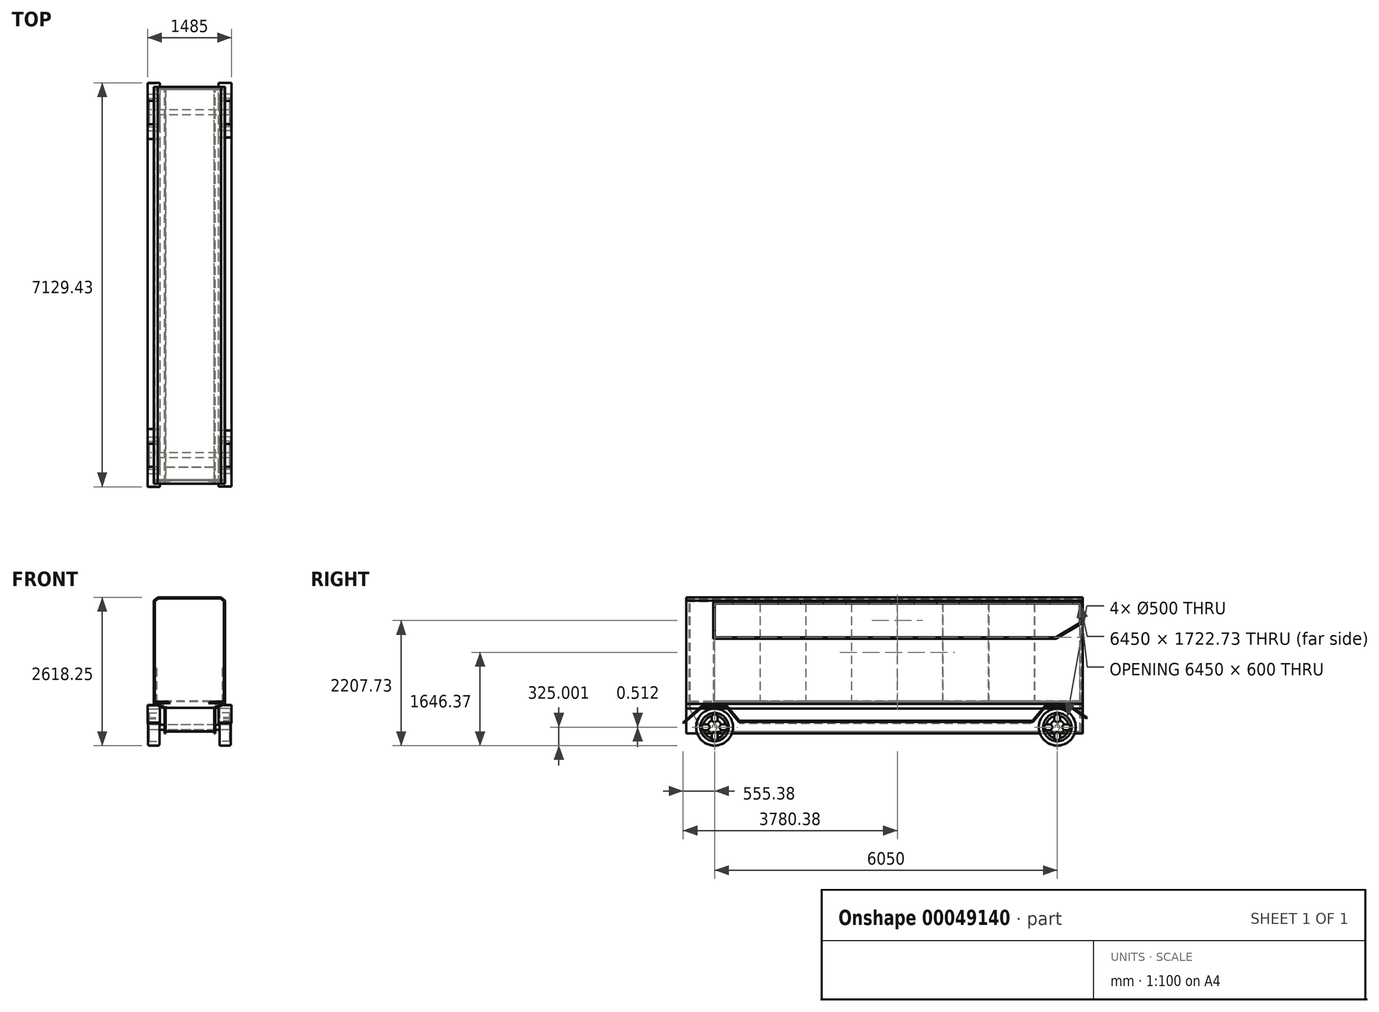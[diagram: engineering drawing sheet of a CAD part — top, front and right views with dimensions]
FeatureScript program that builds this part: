
annotation { "Feature Type Name" : "Feature", "Feature Type Description" : "" }
export const myFeature = defineFeature(function(context is Context, id is Id, definition is map)
    precondition{}
    {
        {
            var Q0;
            Q0=qCreatedBy(makeId("Front.planeOp"),FACE);
            var sketch = newSketch(context, id + "F0", { "sketchPlane" : qUnion([Q0])});
            skLineSegment(sketch, "E0", {"start": v(0, 0) * mm, "end": v(0, 1850) * mm, "construction": true});
            skLineSegment(sketch, "E1", {"start": v(-548.86, 1850) * mm, "end": v(548.86, 1850) * mm});
            skLineSegment(sketch, "E2", {"start": v(-610, 1800) * mm, "end": v(-610, 0) * mm});
            skLineSegment(sketch, "E3", {"start": v(610, 1800) * mm, "end": v(610, 0) * mm});
            skLineSegment(sketch, "E4", {"start": v(-548.86, 1850) * mm, "end": v(-610, 1800) * mm});
            skLineSegment(sketch, "E5", {"start": v(548.86, 1850) * mm, "end": v(610, 1800) * mm});
            skLineSegment(sketch, "E6", {"start": v(-610, 0) * mm, "end": v(-421.1, -80) * mm});
            skLineSegment(sketch, "E7", {"start": v(-421.1, -80) * mm, "end": v(-421.1, -530) * mm});
            skLineSegment(sketch, "E8", {"start": v(610, 0) * mm, "end": v(438.57, -80) * mm});
            skLineSegment(sketch, "E9", {"start": v(438.57, -80) * mm, "end": v(438.57, -530) * mm});
            skLineSegment(sketch, "E10.0", {"start": v(-441.1, -93.25) * mm, "end": v(-441.1, -530) * mm});
            skLineSegment(sketch, "E10.1", {"start": v(-630, -13.25) * mm, "end": v(-441.1, -93.25) * mm});
            skLineSegment(sketch, "E10.2", {"start": v(-630, 1809.48) * mm, "end": v(-630, -13.25) * mm});
            skLineSegment(sketch, "E10.3", {"start": v(-556, 1870) * mm, "end": v(-630, 1809.48) * mm});
            skLineSegment(sketch, "E10.4", {"start": v(-556, 1870) * mm, "end": v(556, 1870) * mm});
            skLineSegment(sketch, "E10.5", {"start": v(458.57, -92.74) * mm, "end": v(458.57, -530) * mm});
            skLineSegment(sketch, "E10.6", {"start": v(630, -12.74) * mm, "end": v(458.57, -92.74) * mm});
            skLineSegment(sketch, "E10.7", {"start": v(630, 1809.48) * mm, "end": v(630, -12.74) * mm});
            skLineSegment(sketch, "E10.8", {"start": v(556, 1870) * mm, "end": v(630, 1809.48) * mm});
            skLineSegment(sketch, "E11", {"start": v(-441.1, -530) * mm, "end": v(-421.1, -530) * mm});
            skLineSegment(sketch, "E12", {"start": v(438.57, -530) * mm, "end": v(458.57, -530) * mm});
            skSolve(sketch);
        }
        {
            var Q0;
            Q0 = qSketchRegion(id + "F0", true);
            extrude(context, id + "F1", {"entities" : qUnion([Q0]), "depth" : 7000 * mm});
        }
        {
            var Q0;
            Q0=makeQuery(id+"F1.opExtrude","SWEPT_FACE",FACE,{"disambiguationData":[OSD([sQuery(id+"F0.wireOp",EDGE,"E3")])]});
            var sketch = newSketch(context, id + "F2", { "sketchPlane" : qUnion([Q0])});
            skLineSegment(sketch, "E13.bottom", {"start": v(6930, 1800) * mm, "end": v(6950, 1800) * mm});
            skLineSegment(sketch, "E13.top", {"start": v(6930, 0) * mm, "end": v(6950, 0) * mm});
            skLineSegment(sketch, "E13.left", {"start": v(6930, 1800) * mm, "end": v(6930, 0) * mm});
            skLineSegment(sketch, "E13.right", {"start": v(6950, 1800) * mm, "end": v(6950, 0) * mm});
            skSolve(sketch);
        }
        {
            var Q0;
            Q0 = qSketchRegion(id + "F2", true);
            extrude(context, id + "F3", {"entities" : qUnion([Q0]), "endBound" : BoundingType.UP_TO_NEXT, "depth" : 25 * mm});
        }
        {
            var Q0;
            Q0=makeQuery(id+"F3.opExtrude","SWEPT_FACE",FACE,{"disambiguationData":[OSD([sQuery(id+"F2.wireOp",EDGE,"E13.right")])]});
            var sketch = newSketch(context, id + "F4", { "sketchPlane" : qUnion([Q0])});
            skLineSegment(sketch, "E14", {"start": v(-610, 1800) * mm, "end": v(610, 1800) * mm});
            skLineSegment(sketch, "E15", {"start": v(610, 1800) * mm, "end": v(549.02, 1850.83) * mm});
            skLineSegment(sketch, "E16", {"start": v(549.02, 1850.83) * mm, "end": v(-548.33, 1850.83) * mm});
            skLineSegment(sketch, "E17", {"start": v(-548.33, 1850.83) * mm, "end": v(-610, 1800) * mm});
            skSolve(sketch);
        }
        {
            var Q0;
            Q0 = qSketchRegion(id + "F4", true);
            extrude(context, id + "F5", {"entities" : qUnion([Q0]), "oppositeDirection" : true, "depth" : 20 * mm});
        }
        {
            var Q0;
            Q0=makeQuery(id+"F5.boolean.opBoolean","MERGE",FACE,{"derivedFrom":[makeQuery(id+"F3.opExtrude","SWEPT_FACE",FACE,{"disambiguationData":[OSD([sQuery(id+"F2.wireOp",EDGE,"E13.right")])]}),makeQuery(id+"F5.opExtrude","CAP_FACE",FACE,{"disambiguationData":[OSD([sQuery(id+"F4.wireOp",EDGE,"E14"),sQuery(id+"F4.wireOp",EDGE,"E15"),sQuery(id+"F4.wireOp",EDGE,"E16"),sQuery(id+"F4.wireOp",EDGE,"E17")])],"isStart":true})]});
            var sketch = newSketch(context, id + "F6", { "sketchPlane" : qUnion([Q0])});
            skLineSegment(sketch, "E18", {"start": v(-610, 0) * mm, "end": v(610, 0) * mm});
            skLineSegment(sketch, "E19", {"start": v(610, 0) * mm, "end": v(438.54, -79.98) * mm});
            skLineSegment(sketch, "E20", {"start": v(438.54, -79.98) * mm, "end": v(438.54, -80.03) * mm});
            skLineSegment(sketch, "E21", {"start": v(438.54, -80.03) * mm, "end": v(-421.13, -80.03) * mm});
            skLineSegment(sketch, "E22", {"start": v(-421.13, -80.03) * mm, "end": v(-421.13, -79.98) * mm});
            skLineSegment(sketch, "E23", {"start": v(-421.13, -79.98) * mm, "end": v(-610, 0) * mm});
            skSolve(sketch);
        }
        {
            var Q0;
            Q0 = qSketchRegion(id + "F6", true);
            extrude(context, id + "F7", {"entities" : qUnion([Q0]), "oppositeDirection" : true, "depth" : 20 * mm});
        }
        {
            var Q0;
            Q0=makeQuery(id+"F1.opExtrude","SWEPT_FACE",FACE,{"disambiguationData":[OSD([sQuery(id+"F0.wireOp",EDGE,"E10.2")])]});
            var sketch = newSketch(context, id + "F8", { "sketchPlane" : qUnion([Q0])});
            skLineSegment(sketch, "E24.bottom", {"start": v(50, 1759.48) * mm, "end": v(6500, 1759.48) * mm});
            skLineSegment(sketch, "E24.top", {"start": v(50, 36.75) * mm, "end": v(6500, 36.75) * mm});
            skLineSegment(sketch, "E24.left", {"start": v(50, 1759.48) * mm, "end": v(50, 36.75) * mm});
            skLineSegment(sketch, "E24.right", {"start": v(6500, 1759.48) * mm, "end": v(6500, 36.75) * mm});
            skSolve(sketch);
        }
        {
            var Q0;
            Q0=makeQuery(id+"F8.imprint","IMPRINT",FACE,{"disambiguationData":[TD([[makeQuery(id+"F8.imprint","IMPRINT",EDGE,{"derivedFrom":sQuery(id+"F8.wireOp",EDGE,"E24.bottom")}),-1.0]])]});
            extrude(context, id + "F9", {"entities" : qUnion([Q0]), "operationType" : NewBodyOperationType.REMOVE, "oppositeDirection" : true, "depth" : 25 * mm});
        }
        {
            var Q0;
            Q0=makeQuery(id+"F3.opExtrude","SWEPT_BODY",BODY,{"disambiguationData":[OSD([sQuery(id+"F2.wireOp",EDGE,"E13.bottom"),sQuery(id+"F2.wireOp",EDGE,"E13.top"),sQuery(id+"F2.wireOp",EDGE,"E13.left"),sQuery(id+"F2.wireOp",EDGE,"E13.right")])]});
            var Q1;
            Q1=makeQuery(id+"F7.opExtrude","SWEPT_BODY",BODY,{"disambiguationData":[OSD([sQuery(id+"F6.wireOp",EDGE,"E18"),sQuery(id+"F6.wireOp",EDGE,"E19"),sQuery(id+"F6.wireOp",EDGE,"E20"),sQuery(id+"F6.wireOp",EDGE,"E21"),sQuery(id+"F6.wireOp",EDGE,"E22"),sQuery(id+"F6.wireOp",EDGE,"E23")])]});
            var Q2;
            Q2=makeQuery(id+"F5.opExtrude","SWEPT_BODY",BODY,{"disambiguationData":[OSD([sQuery(id+"F4.wireOp",EDGE,"E14"),sQuery(id+"F4.wireOp",EDGE,"E15"),sQuery(id+"F4.wireOp",EDGE,"E16"),sQuery(id+"F4.wireOp",EDGE,"E17")])]});
            booleanBodies(context, id + "F10", {"operationType" : BooleanOperationType.UNION, "tools" : qUnion([Q0, Q1, Q2])});
        }
        {
            var Q0;
            Q0=makeQuery(id+"F1.opExtrude","SWEPT_FACE",FACE,{"disambiguationData":[OSD([sQuery(id+"F0.wireOp",EDGE,"E2")])]});
            var sketch = newSketch(context, id + "F11", { "sketchPlane" : qUnion([Q0])});
            skLineSegment(sketch, "E25.bottom", {"start": v(-50, 1800) * mm, "end": v(-30, 1800) * mm});
            skLineSegment(sketch, "E25.top", {"start": v(-50, 0) * mm, "end": v(-30, 0) * mm});
            skLineSegment(sketch, "E25.left", {"start": v(-50, 1800) * mm, "end": v(-50, 0) * mm});
            skLineSegment(sketch, "E25.right", {"start": v(-30, 1800) * mm, "end": v(-30, 0) * mm});
            skSolve(sketch);
        }
        {
            var Q0;
            Q0 = qSketchRegion(id + "F11", true);
            extrude(context, id + "F12", {"entities" : qUnion([Q0]), "operationType" : NewBodyOperationType.ADD, "endBound" : BoundingType.UP_TO_NEXT, "depth" : 25 * mm});
        }
        {
            var Q0;
            Q0=makeQuery(id+"F12.opExtrude","SWEPT_FACE",FACE,{"disambiguationData":[OSD([sQuery(id+"F11.wireOp",EDGE,"E25.right")])]});
            var sketch = newSketch(context, id + "F13", { "sketchPlane" : qUnion([Q0])});
            skLineSegment(sketch, "E26", {"start": v(-610, 1800) * mm, "end": v(610, 1800) * mm});
            skLineSegment(sketch, "E27", {"start": v(610, 1800) * mm, "end": v(548.9, 1850.1) * mm});
            skLineSegment(sketch, "E28", {"start": v(548.9, 1850.1) * mm, "end": v(-548.85, 1850.1) * mm});
            skLineSegment(sketch, "E29", {"start": v(-548.85, 1850.1) * mm, "end": v(-610, 1800) * mm});
            skSolve(sketch);
        }
        {
            var Q0;
            Q0 = qSketchRegion(id + "F13", true);
            extrude(context, id + "F14", {"entities" : qUnion([Q0]), "operationType" : NewBodyOperationType.ADD, "oppositeDirection" : true, "depth" : 20 * mm});
        }
        {
            var Q0;
            Q0=makeQuery(id+"F14.boolean.opBoolean","MERGE",FACE,{"derivedFrom":[makeQuery(id+"F12.opExtrude","SWEPT_FACE",FACE,{"disambiguationData":[OSD([sQuery(id+"F11.wireOp",EDGE,"E25.right")])]}),makeQuery(id+"F14.opExtrude","CAP_FACE",FACE,{"disambiguationData":[OSD([sQuery(id+"F13.wireOp",EDGE,"E26"),sQuery(id+"F13.wireOp",EDGE,"E27"),sQuery(id+"F13.wireOp",EDGE,"E28"),sQuery(id+"F13.wireOp",EDGE,"E29")])],"isStart":true})]});
            var sketch = newSketch(context, id + "F15", { "sketchPlane" : qUnion([Q0])});
            skLineSegment(sketch, "E30", {"start": v(-610, 0) * mm, "end": v(610, 0) * mm});
            skLineSegment(sketch, "E31", {"start": v(610, 0) * mm, "end": v(421.14, -80.03) * mm});
            skLineSegment(sketch, "E32", {"start": v(421.14, -80.03) * mm, "end": v(421.14, -504.23) * mm});
            skLineSegment(sketch, "E33", {"start": v(421.14, -504.23) * mm, "end": v(-438.57, -504.23) * mm});
            skLineSegment(sketch, "E34", {"start": v(-438.57, -504.23) * mm, "end": v(-438.57, -80.03) * mm});
            skLineSegment(sketch, "E35", {"start": v(-438.57, -80.03) * mm, "end": v(-610, 0) * mm});
            skSolve(sketch);
        }
        {
            var Q0;
            Q0 = qSketchRegion(id + "F15", true);
            extrude(context, id + "F16", {"entities" : qUnion([Q0]), "operationType" : NewBodyOperationType.ADD, "oppositeDirection" : true, "depth" : 20 * mm});
        }
        {
            var Q0;
            Q0=makeQuery(id+"F16.boolean.opBoolean","MERGE",FACE,{"derivedFrom":[makeQuery(id+"F14.boolean.opBoolean","MERGE",FACE,{"derivedFrom":[makeQuery(id+"F12.boolean.opBoolean","MERGE",FACE,{"derivedFrom":[makeQuery(id+"F9.boolean.opBoolean","COPY",FACE,{"derivedFrom":makeQuery(id+"F9.opExtrude","SWEPT_FACE",FACE,{"disambiguationData":[OSD([sQuery(id+"F8.wireOp",EDGE,"E24.left")])]})}),makeQuery(id+"F12.opExtrude","SWEPT_FACE",FACE,{"disambiguationData":[OSD([sQuery(id+"F11.wireOp",EDGE,"E25.left")])]})]}),makeQuery(id+"F14.opExtrude","CAP_FACE",FACE,{"disambiguationData":[OSD([sQuery(id+"F13.wireOp",EDGE,"E26"),sQuery(id+"F13.wireOp",EDGE,"E27"),sQuery(id+"F13.wireOp",EDGE,"E28"),sQuery(id+"F13.wireOp",EDGE,"E29")])],"isStart":false})]}),makeQuery(id+"F16.opExtrude","CAP_FACE",FACE,{"disambiguationData":[OSD([sQuery(id+"F15.wireOp",EDGE,"E30"),sQuery(id+"F15.wireOp",EDGE,"E31"),sQuery(id+"F15.wireOp",EDGE,"E32"),sQuery(id+"F15.wireOp",EDGE,"E33"),sQuery(id+"F15.wireOp",EDGE,"E34"),sQuery(id+"F15.wireOp",EDGE,"E35")])],"isStart":false})]});
            var sketch = newSketch(context, id + "F17", { "sketchPlane" : qUnion([Q0])});
            skLineSegment(sketch, "E36.bottom", {"start": v(610, 26.75) * mm, "end": v(-610, 26.75) * mm});
            skLineSegment(sketch, "E36.top", {"start": v(610, 36.75) * mm, "end": v(-610, 36.75) * mm});
            skLineSegment(sketch, "E36.left", {"start": v(610, 26.75) * mm, "end": v(610, 36.75) * mm});
            skLineSegment(sketch, "E36.right", {"start": v(-610, 26.75) * mm, "end": v(-610, 36.75) * mm});
            skLineSegment(sketch, "E37.bottom", {"start": v(438.57, -504.23) * mm, "end": v(-421.1, -504.23) * mm});
            skLineSegment(sketch, "E37.top", {"start": v(438.57, -494.23) * mm, "end": v(-421.1, -494.23) * mm});
            skLineSegment(sketch, "E37.left", {"start": v(438.57, -504.23) * mm, "end": v(438.57, -494.23) * mm});
            skLineSegment(sketch, "E37.right", {"start": v(-421.1, -504.23) * mm, "end": v(-421.1, -494.23) * mm});
            skSolve(sketch);
        }
        {
            var Q0;
            Q0 = qSketchRegion(id + "F17", true);
            var Q1;
            Q1=makeQuery(id+"F10.opBoolean","MERGE",FACE,{"derivedFrom":[makeQuery(id+"F3.opExtrude","SWEPT_FACE",FACE,{"disambiguationData":[OSD([sQuery(id+"F2.wireOp",EDGE,"E13.left")])]}),makeQuery(id+"F5.opExtrude","CAP_FACE",FACE,{"disambiguationData":[OSD([sQuery(id+"F4.wireOp",EDGE,"E14"),sQuery(id+"F4.wireOp",EDGE,"E15"),sQuery(id+"F4.wireOp",EDGE,"E16"),sQuery(id+"F4.wireOp",EDGE,"E17")])],"isStart":false}),makeQuery(id+"F7.opExtrude","CAP_FACE",FACE,{"disambiguationData":[OSD([sQuery(id+"F6.wireOp",EDGE,"E18"),sQuery(id+"F6.wireOp",EDGE,"E19"),sQuery(id+"F6.wireOp",EDGE,"E20"),sQuery(id+"F6.wireOp",EDGE,"E21"),sQuery(id+"F6.wireOp",EDGE,"E22"),sQuery(id+"F6.wireOp",EDGE,"E23")])],"isStart":false})]});
            extrude(context, id + "F18", {"entities" : qUnion([Q0]), "endBound" : BoundingType.UP_TO_SURFACE, "endBoundEntityFace" : qUnion([Q1]), "depth" : 6874.52 * mm});
        }
        {
            var Q0;
            Q0=makeQuery(id+"F1.opExtrude","SWEPT_BODY",BODY,{"disambiguationData":[OSD([sQuery(id+"F0.wireOp",EDGE,"E1"),sQuery(id+"F0.wireOp",EDGE,"E2"),sQuery(id+"F0.wireOp",EDGE,"E3"),sQuery(id+"F0.wireOp",EDGE,"E4"),sQuery(id+"F0.wireOp",EDGE,"E5"),sQuery(id+"F0.wireOp",EDGE,"E6"),sQuery(id+"F0.wireOp",EDGE,"E7"),sQuery(id+"F0.wireOp",EDGE,"E8"),sQuery(id+"F0.wireOp",EDGE,"E9"),sQuery(id+"F0.wireOp",EDGE,"E10.0"),sQuery(id+"F0.wireOp",EDGE,"E10.1"),sQuery(id+"F0.wireOp",EDGE,"E10.2"),sQuery(id+"F0.wireOp",EDGE,"E10.3"),sQuery(id+"F0.wireOp",EDGE,"E10.4"),sQuery(id+"F0.wireOp",EDGE,"E10.5"),sQuery(id+"F0.wireOp",EDGE,"E10.6"),sQuery(id+"F0.wireOp",EDGE,"E10.7"),sQuery(id+"F0.wireOp",EDGE,"E10.8"),sQuery(id+"F0.wireOp",EDGE,"E11"),sQuery(id+"F0.wireOp",EDGE,"E12")])]});
            var Q1;
            Q1=makeQuery(id+"F18.opExtrude","SWEPT_BODY",BODY,{"disambiguationData":[OSD([sQuery(id+"F17.wireOp",EDGE,"E36.bottom"),sQuery(id+"F17.wireOp",EDGE,"E36.top"),sQuery(id+"F17.wireOp",EDGE,"E36.left"),sQuery(id+"F17.wireOp",EDGE,"E36.right")])]});
            var Q2;
            Q2=makeQuery(id+"F18.opExtrude","SWEPT_BODY",BODY,{"disambiguationData":[OSD([sQuery(id+"F17.wireOp",EDGE,"E37.bottom"),sQuery(id+"F17.wireOp",EDGE,"E37.top"),sQuery(id+"F17.wireOp",EDGE,"E37.left"),sQuery(id+"F17.wireOp",EDGE,"E37.right")])]});
            booleanBodies(context, id + "F19", {"operationType" : BooleanOperationType.UNION, "tools" : qUnion([Q0, Q1, Q2])});
        }
        {
            var Q0;
            Q0=makeQuery(id+"F1.opExtrude","SWEPT_FACE",FACE,{"disambiguationData":[OSD([sQuery(id+"F0.wireOp",EDGE,"E10.2")])]});
            var sketch = newSketch(context, id + "F20", { "sketchPlane" : qUnion([Q0])});
            skLineSegment(sketch, "E38.bottom", {"start": v(50, 1759.48) * mm, "end": v(855, 1759.48) * mm});
            skLineSegment(sketch, "E38.top", {"start": v(50, 36.75) * mm, "end": v(855, 36.75) * mm});
            skLineSegment(sketch, "E38.left", {"start": v(50, 1759.48) * mm, "end": v(50, 36.75) * mm});
            skLineSegment(sketch, "E38.right", {"start": v(855, 1759.48) * mm, "end": v(855, 36.75) * mm});
            skLineSegment(sketch, "E39.bottom", {"start": v(857, 1759.48) * mm, "end": v(1662, 1759.48) * mm});
            skLineSegment(sketch, "E39.top", {"start": v(857, 36.75) * mm, "end": v(1662, 36.75) * mm});
            skLineSegment(sketch, "E39.left", {"start": v(857, 1759.48) * mm, "end": v(857, 36.75) * mm});
            skLineSegment(sketch, "E39.right", {"start": v(1662, 1759.48) * mm, "end": v(1662, 36.75) * mm});
            skLineSegment(sketch, "E40.bottom", {"start": v(1664, 36.75) * mm, "end": v(2469, 36.75) * mm});
            skLineSegment(sketch, "E40.top", {"start": v(1664, 1759.48) * mm, "end": v(2469, 1759.48) * mm});
            skLineSegment(sketch, "E40.left", {"start": v(1664, 36.75) * mm, "end": v(1664, 1759.48) * mm});
            skLineSegment(sketch, "E40.right", {"start": v(2469, 36.75) * mm, "end": v(2469, 1759.48) * mm});
            skLineSegment(sketch, "E41.bottom", {"start": v(2471, 1759.48) * mm, "end": v(3276, 1759.48) * mm});
            skLineSegment(sketch, "E41.top", {"start": v(2471, 36.75) * mm, "end": v(3276, 36.75) * mm});
            skLineSegment(sketch, "E41.left", {"start": v(2471, 1759.48) * mm, "end": v(2471, 36.75) * mm});
            skLineSegment(sketch, "E41.right", {"start": v(3276, 1759.48) * mm, "end": v(3276, 36.75) * mm});
            skLineSegment(sketch, "E42.bottom", {"start": v(3278, 1759.48) * mm, "end": v(4083, 1759.48) * mm});
            skLineSegment(sketch, "E42.top", {"start": v(3278, 36.75) * mm, "end": v(4083, 36.75) * mm});
            skLineSegment(sketch, "E42.left", {"start": v(3278, 1759.48) * mm, "end": v(3278, 36.75) * mm});
            skLineSegment(sketch, "E42.right", {"start": v(4083, 1759.48) * mm, "end": v(4083, 36.75) * mm});
            skLineSegment(sketch, "E43.bottom", {"start": v(4085, 1759.48) * mm, "end": v(4890, 1759.48) * mm});
            skLineSegment(sketch, "E43.top", {"start": v(4085, 36.75) * mm, "end": v(4890, 36.75) * mm});
            skLineSegment(sketch, "E43.left", {"start": v(4085, 1759.48) * mm, "end": v(4085, 36.75) * mm});
            skLineSegment(sketch, "E43.right", {"start": v(4890, 1759.48) * mm, "end": v(4890, 36.75) * mm});
            skLineSegment(sketch, "E44.bottom", {"start": v(4892, 1759.48) * mm, "end": v(5697, 1759.48) * mm});
            skLineSegment(sketch, "E44.top", {"start": v(4892, 36.75) * mm, "end": v(5697, 36.75) * mm});
            skLineSegment(sketch, "E44.left", {"start": v(4892, 1759.48) * mm, "end": v(4892, 36.75) * mm});
            skLineSegment(sketch, "E44.right", {"start": v(5697, 1759.48) * mm, "end": v(5697, 36.75) * mm});
            skLineSegment(sketch, "E45.bottom", {"start": v(5699, 1759.48) * mm, "end": v(6504, 1759.48) * mm});
            skLineSegment(sketch, "E45.top", {"start": v(5699, 36.75) * mm, "end": v(6504, 36.75) * mm});
            skLineSegment(sketch, "E45.left", {"start": v(5699, 1759.48) * mm, "end": v(5699, 36.75) * mm});
            skLineSegment(sketch, "E45.right", {"start": v(6504, 1759.48) * mm, "end": v(6504, 36.75) * mm});
            skSolve(sketch);
        }
        {
            var Q0;
            Q0 = qSketchRegion(id + "F20", true);
            extrude(context, id + "F21", {"entities" : qUnion([Q0]), "oppositeDirection" : true, "depth" : 20 * mm});
        }
        {
            var Q0;
            Q0=makeQuery(id+"F1.opExtrude","CAP_FACE",FACE,{"disambiguationData":[OSD([sQuery(id+"F0.wireOp",EDGE,"E1"),sQuery(id+"F0.wireOp",EDGE,"E2"),sQuery(id+"F0.wireOp",EDGE,"E3"),sQuery(id+"F0.wireOp",EDGE,"E4"),sQuery(id+"F0.wireOp",EDGE,"E5"),sQuery(id+"F0.wireOp",EDGE,"E6"),sQuery(id+"F0.wireOp",EDGE,"E7"),sQuery(id+"F0.wireOp",EDGE,"E8"),sQuery(id+"F0.wireOp",EDGE,"E9"),sQuery(id+"F0.wireOp",EDGE,"E10.0"),sQuery(id+"F0.wireOp",EDGE,"E10.1"),sQuery(id+"F0.wireOp",EDGE,"E10.2"),sQuery(id+"F0.wireOp",EDGE,"E10.3"),sQuery(id+"F0.wireOp",EDGE,"E10.4"),sQuery(id+"F0.wireOp",EDGE,"E10.5"),sQuery(id+"F0.wireOp",EDGE,"E10.6"),sQuery(id+"F0.wireOp",EDGE,"E10.7"),sQuery(id+"F0.wireOp",EDGE,"E10.8"),sQuery(id+"F0.wireOp",EDGE,"E11"),sQuery(id+"F0.wireOp",EDGE,"E12")])],"isStart":false});
            var sketch = newSketch(context, id + "F22", { "sketchPlane" : qUnion([Q0])});
            skLineSegment(sketch, "E46", {"start": v(-556, 1870) * mm, "end": v(556, 1870) * mm});
            skLineSegment(sketch, "E47", {"start": v(556, 1870) * mm, "end": v(630, 1809.48) * mm});
            skLineSegment(sketch, "E48", {"start": v(630, 1809.48) * mm, "end": v(630, -12.74) * mm});
            skLineSegment(sketch, "E49", {"start": v(630, -12.74) * mm, "end": v(458.57, -92.74) * mm});
            skLineSegment(sketch, "E50", {"start": v(458.57, -92.74) * mm, "end": v(458.57, -530) * mm});
            skLineSegment(sketch, "E51", {"start": v(458.57, -530) * mm, "end": v(438.57, -530) * mm});
            skLineSegment(sketch, "E52", {"start": v(438.57, -530) * mm, "end": v(438.57, -80) * mm});
            skLineSegment(sketch, "E53", {"start": v(438.57, -80) * mm, "end": v(610, 0) * mm});
            skLineSegment(sketch, "E54", {"start": v(610, 0) * mm, "end": v(610, 1800) * mm});
            skLineSegment(sketch, "E55", {"start": v(610, 1800) * mm, "end": v(548.86, 1850) * mm});
            skLineSegment(sketch, "E56", {"start": v(548.86, 1850) * mm, "end": v(-548.86, 1850) * mm});
            skLineSegment(sketch, "E57", {"start": v(-548.86, 1850) * mm, "end": v(-610, 1800) * mm});
            skLineSegment(sketch, "E58", {"start": v(-610, 1800) * mm, "end": v(-610, 0) * mm});
            skLineSegment(sketch, "E59", {"start": v(-610, 0) * mm, "end": v(-421.1, -80) * mm});
            skLineSegment(sketch, "E60", {"start": v(-421.1, -80) * mm, "end": v(-421.1, -530) * mm});
            skLineSegment(sketch, "E61", {"start": v(-421.1, -530) * mm, "end": v(-441.1, -530) * mm});
            skLineSegment(sketch, "E62", {"start": v(-441.1, -530) * mm, "end": v(-441.1, -93.25) * mm});
            skLineSegment(sketch, "E63", {"start": v(-441.1, -93.25) * mm, "end": v(-630, -13.25) * mm});
            skLineSegment(sketch, "E64", {"start": v(-630, -13.25) * mm, "end": v(-630, 1809.48) * mm});
            skLineSegment(sketch, "E65", {"start": v(-630, 1809.48) * mm, "end": v(-556, 1870) * mm});
            skSolve(sketch);
        }
        {
            var Q0;
            Q0 = qSketchRegion(id + "F22", true);
            extrude(context, id + "F23", {"entities" : qUnion([Q0]), "depth" : 1 * mm});
        }
        {
            var Q0;
            Q0=makeQuery(id+"F1.opExtrude","CAP_FACE",FACE,{"disambiguationData":[OSD([sQuery(id+"F0.wireOp",EDGE,"E1"),sQuery(id+"F0.wireOp",EDGE,"E2"),sQuery(id+"F0.wireOp",EDGE,"E3"),sQuery(id+"F0.wireOp",EDGE,"E4"),sQuery(id+"F0.wireOp",EDGE,"E5"),sQuery(id+"F0.wireOp",EDGE,"E6"),sQuery(id+"F0.wireOp",EDGE,"E7"),sQuery(id+"F0.wireOp",EDGE,"E8"),sQuery(id+"F0.wireOp",EDGE,"E9"),sQuery(id+"F0.wireOp",EDGE,"E10.0"),sQuery(id+"F0.wireOp",EDGE,"E10.1"),sQuery(id+"F0.wireOp",EDGE,"E10.2"),sQuery(id+"F0.wireOp",EDGE,"E10.3"),sQuery(id+"F0.wireOp",EDGE,"E10.4"),sQuery(id+"F0.wireOp",EDGE,"E10.5"),sQuery(id+"F0.wireOp",EDGE,"E10.6"),sQuery(id+"F0.wireOp",EDGE,"E10.7"),sQuery(id+"F0.wireOp",EDGE,"E10.8"),sQuery(id+"F0.wireOp",EDGE,"E11"),sQuery(id+"F0.wireOp",EDGE,"E12")])],"isStart":true});
            var sketch = newSketch(context, id + "F24", { "sketchPlane" : qUnion([Q0])});
            skLineSegment(sketch, "E66", {"start": v(-556, 1870) * mm, "end": v(556, 1870) * mm});
            skLineSegment(sketch, "E67", {"start": v(556, 1870) * mm, "end": v(630, 1809.48) * mm});
            skLineSegment(sketch, "E68", {"start": v(630, 1809.48) * mm, "end": v(630, -13.25) * mm});
            skLineSegment(sketch, "E69", {"start": v(630, -13.25) * mm, "end": v(441.1, -93.25) * mm});
            skLineSegment(sketch, "E70", {"start": v(441.1, -93.25) * mm, "end": v(441.1, -530) * mm});
            skLineSegment(sketch, "E71", {"start": v(441.1, -530) * mm, "end": v(421.1, -530) * mm});
            skLineSegment(sketch, "E72", {"start": v(421.1, -530) * mm, "end": v(421.1, -80) * mm});
            skLineSegment(sketch, "E73", {"start": v(421.1, -80) * mm, "end": v(610, 0) * mm});
            skLineSegment(sketch, "E74", {"start": v(610, 0) * mm, "end": v(610, 1800) * mm});
            skLineSegment(sketch, "E75", {"start": v(610, 1800) * mm, "end": v(548.86, 1850) * mm});
            skLineSegment(sketch, "E76", {"start": v(548.86, 1850) * mm, "end": v(-548.86, 1850) * mm});
            skLineSegment(sketch, "E77", {"start": v(-548.86, 1850) * mm, "end": v(-610, 1800) * mm});
            skLineSegment(sketch, "E78", {"start": v(-610, 1800) * mm, "end": v(-610, 0) * mm});
            skLineSegment(sketch, "E79", {"start": v(-610, 0) * mm, "end": v(-438.57, -80) * mm});
            skLineSegment(sketch, "E80", {"start": v(-438.57, -80) * mm, "end": v(-438.57, -530) * mm});
            skLineSegment(sketch, "E81", {"start": v(-438.57, -530) * mm, "end": v(-458.57, -530) * mm});
            skLineSegment(sketch, "E82", {"start": v(-458.57, -530) * mm, "end": v(-458.57, -92.74) * mm});
            skLineSegment(sketch, "E83", {"start": v(-458.57, -92.74) * mm, "end": v(-630, -12.74) * mm});
            skLineSegment(sketch, "E84", {"start": v(-630, -12.74) * mm, "end": v(-630, 1809.48) * mm});
            skLineSegment(sketch, "E85", {"start": v(-630, 1809.48) * mm, "end": v(-556, 1870) * mm});
            skSolve(sketch);
        }
        {
            var Q0;
            Q0 = qSketchRegion(id + "F24", true);
            extrude(context, id + "F25", {"entities" : qUnion([Q0]), "depth" : 1 * mm});
        }
        {
            var Q0;
            Q0=makeQuery(id+"F1.opExtrude","SWEPT_FACE",FACE,{"disambiguationData":[OSD([sQuery(id+"F0.wireOp",EDGE,"E10.7")])]});
            var sketch = newSketch(context, id + "F26", { "sketchPlane" : qUnion([Q0])});
            skLineSegment(sketch, "E86.bottom", {"start": v(-50, 1759.48) * mm, "end": v(-6500, 1759.48) * mm});
            skLineSegment(sketch, "E86.top", {"start": v(-480.24, 1159.48) * mm, "end": v(-6500, 1159.48) * mm});
            skLineSegment(sketch, "E86.left", {"start": v(-50, 1759.48) * mm, "end": v(-50, 1414.22) * mm});
            skLineSegment(sketch, "E86.right", {"start": v(-6500, 1759.48) * mm, "end": v(-6500, 1159.48) * mm});
            skLineSegment(sketch, "E87", {"start": v(-480.24, 1159.48) * mm, "end": v(-50, 1414.22) * mm});
            skSolve(sketch);
        }
        {
            var Q0;
            Q0 = qSketchRegion(id + "F26", true);
            extrude(context, id + "F27", {"entities" : qUnion([Q0]), "operationType" : NewBodyOperationType.REMOVE, "oppositeDirection" : true, "depth" : 25 * mm});
        }
        {
            var Q0;
            Q0=makeQuery(id+"F1.opExtrude","SWEPT_FACE",FACE,{"disambiguationData":[OSD([sQuery(id+"F0.wireOp",EDGE,"E10.7")])]});
            var sketch = newSketch(context, id + "F28", { "sketchPlane" : qUnion([Q0])});
            skLineSegment(sketch, "E88", {"start": v(-6500, 1759.48) * mm, "end": v(-6500, 1159.48) * mm});
            skLineSegment(sketch, "E89", {"start": v(-6500, 1159.48) * mm, "end": v(-480.24, 1159.48) * mm});
            skLineSegment(sketch, "E90", {"start": v(-480.24, 1159.48) * mm, "end": v(-50, 1414.22) * mm});
            skLineSegment(sketch, "E91", {"start": v(-50, 1414.22) * mm, "end": v(-50, 1759.48) * mm});
            skLineSegment(sketch, "E92", {"start": v(-50, 1759.48) * mm, "end": v(-6500, 1759.48) * mm});
            skSolve(sketch);
        }
        {
            var Q0;
            Q0 = qSketchRegion(id + "F28", true);
            extrude(context, id + "F29", {"entities" : qUnion([Q0]), "oppositeDirection" : true, "depth" : 20 * mm});
        }
        {
            var Q0;
            Q0=makeQuery(id+"F16.boolean.opBoolean","MERGE",FACE,{"derivedFrom":[makeQuery(id+"F14.boolean.opBoolean","MERGE",FACE,{"derivedFrom":[makeQuery(id+"F12.opExtrude","SWEPT_FACE",FACE,{"disambiguationData":[OSD([sQuery(id+"F11.wireOp",EDGE,"E25.right")])]}),makeQuery(id+"F14.opExtrude","CAP_FACE",FACE,{"disambiguationData":[OSD([sQuery(id+"F13.wireOp",EDGE,"E26"),sQuery(id+"F13.wireOp",EDGE,"E27"),sQuery(id+"F13.wireOp",EDGE,"E28"),sQuery(id+"F13.wireOp",EDGE,"E29")])],"isStart":true})]}),makeQuery(id+"F16.opExtrude","CAP_FACE",FACE,{"disambiguationData":[OSD([sQuery(id+"F15.wireOp",EDGE,"E30"),sQuery(id+"F15.wireOp",EDGE,"E31"),sQuery(id+"F15.wireOp",EDGE,"E32"),sQuery(id+"F15.wireOp",EDGE,"E33"),sQuery(id+"F15.wireOp",EDGE,"E34"),sQuery(id+"F15.wireOp",EDGE,"E35")])],"isStart":true})]});
            var sketch = newSketch(context, id + "F30", { "sketchPlane" : qUnion([Q0])});
            skLineSegment(sketch, "E93", {"start": v(-610, 619.1) * mm, "end": v(-610, 0) * mm});
            skLineSegment(sketch, "E94", {"start": v(-610, 0) * mm, "end": v(-438.57, -80) * mm});
            skLineSegment(sketch, "E95.0", {"start": v(-580, 19.1) * mm, "end": v(-425.88, -52.81) * mm});
            skLineSegment(sketch, "E95.1", {"start": v(-580, 619.1) * mm, "end": v(-580, 19.1) * mm});
            skLineSegment(sketch, "E96", {"start": v(-610, 619.1) * mm, "end": v(-580, 619.1) * mm});
            skLineSegment(sketch, "E97", {"start": v(-425.88, -52.81) * mm, "end": v(-438.57, -80) * mm});
            skLineSegment(sketch, "E98", {"start": v(610, 619.1) * mm, "end": v(610, 0) * mm});
            skLineSegment(sketch, "E99", {"start": v(610, 0) * mm, "end": v(421.1, -80) * mm});
            skLineSegment(sketch, "E100.0", {"start": v(580, 19.87) * mm, "end": v(409.4, -52.38) * mm});
            skLineSegment(sketch, "E100.1", {"start": v(580, 619.1) * mm, "end": v(580, 19.87) * mm});
            skLineSegment(sketch, "E101", {"start": v(409.4, -52.38) * mm, "end": v(421.1, -80) * mm});
            skLineSegment(sketch, "E102", {"start": v(580, 619.1) * mm, "end": v(610, 619.1) * mm});
            skSolve(sketch);
        }
        {
            var Q0;
            Q0 = qSketchRegion(id + "F30", true);
            extrude(context, id + "F31", {"entities" : qUnion([Q0]), "depth" : 10 * mm});
        }
        {
            var Q0;
            Q0=makeQuery(id+"F10.opBoolean","MERGE",FACE,{"derivedFrom":[makeQuery(id+"F3.opExtrude","SWEPT_FACE",FACE,{"disambiguationData":[OSD([sQuery(id+"F2.wireOp",EDGE,"E13.right")])]}),makeQuery(id+"F5.opExtrude","CAP_FACE",FACE,{"disambiguationData":[OSD([sQuery(id+"F4.wireOp",EDGE,"E14"),sQuery(id+"F4.wireOp",EDGE,"E15"),sQuery(id+"F4.wireOp",EDGE,"E16"),sQuery(id+"F4.wireOp",EDGE,"E17")])],"isStart":true}),makeQuery(id+"F7.opExtrude","CAP_FACE",FACE,{"disambiguationData":[OSD([sQuery(id+"F6.wireOp",EDGE,"E18"),sQuery(id+"F6.wireOp",EDGE,"E19"),sQuery(id+"F6.wireOp",EDGE,"E20"),sQuery(id+"F6.wireOp",EDGE,"E21"),sQuery(id+"F6.wireOp",EDGE,"E22"),sQuery(id+"F6.wireOp",EDGE,"E23")])],"isStart":true})]});
            var sketch = newSketch(context, id + "F32", { "sketchPlane" : qUnion([Q0])});
            skLineSegment(sketch, "E103", {"start": v(-610, 27.94) * mm, "end": v(-376, 27.94) * mm});
            skLineSegment(sketch, "E104", {"start": v(-376, 27.94) * mm, "end": v(-335.6, 0) * mm});
            skLineSegment(sketch, "E105.0", {"start": v(-382.24, 7.94) * mm, "end": v(-370.76, 0) * mm});
            skLineSegment(sketch, "E105.1", {"start": v(-610, 7.94) * mm, "end": v(-382.24, 7.94) * mm});
            skLineSegment(sketch, "E106", {"start": v(-335.6, 0) * mm, "end": v(-370.76, 0) * mm});
            skLineSegment(sketch, "E107", {"start": v(-610, 7.94) * mm, "end": v(-610, 27.94) * mm});
            skLineSegment(sketch, "E108", {"start": v(610, 27.94) * mm, "end": v(376, 27.94) * mm});
            skLineSegment(sketch, "E109", {"start": v(376, 27.94) * mm, "end": v(335.6, 0) * mm});
            skLineSegment(sketch, "E110.0", {"start": v(382.24, 7.94) * mm, "end": v(370.76, 0) * mm});
            skLineSegment(sketch, "E110.1", {"start": v(610.72, 7.94) * mm, "end": v(382.24, 7.94) * mm});
            skLineSegment(sketch, "E111", {"start": v(335.6, 0) * mm, "end": v(370.76, 0) * mm});
            skLineSegment(sketch, "E112", {"start": v(610, 27.94) * mm, "end": v(610.72, 7.94) * mm});
            skSolve(sketch);
        }
        {
            var Q0;
            Q0 = qSketchRegion(id + "F32", true);
            extrude(context, id + "F33", {"entities" : qUnion([Q0]), "depth" : 5 * mm});
        }
        {
            var Q0;
            Q0=makeQuery(id+"F10.opBoolean","MERGE",FACE,{"derivedFrom":[makeQuery(id+"F3.opExtrude","SWEPT_FACE",FACE,{"disambiguationData":[OSD([sQuery(id+"F2.wireOp",EDGE,"E13.right")])]}),makeQuery(id+"F5.opExtrude","CAP_FACE",FACE,{"disambiguationData":[OSD([sQuery(id+"F4.wireOp",EDGE,"E14"),sQuery(id+"F4.wireOp",EDGE,"E15"),sQuery(id+"F4.wireOp",EDGE,"E16"),sQuery(id+"F4.wireOp",EDGE,"E17")])],"isStart":true}),makeQuery(id+"F7.opExtrude","CAP_FACE",FACE,{"disambiguationData":[OSD([sQuery(id+"F6.wireOp",EDGE,"E18"),sQuery(id+"F6.wireOp",EDGE,"E19"),sQuery(id+"F6.wireOp",EDGE,"E20"),sQuery(id+"F6.wireOp",EDGE,"E21"),sQuery(id+"F6.wireOp",EDGE,"E22"),sQuery(id+"F6.wireOp",EDGE,"E23")])],"isStart":true})]});
            var sketch = newSketch(context, id + "F34", { "sketchPlane" : qUnion([Q0])});
            skLineSegment(sketch, "E113", {"start": v(-522.13, 7.94) * mm, "end": v(-382.13, 7.94) * mm});
            skLineSegment(sketch, "E114", {"start": v(-382.13, 7.94) * mm, "end": v(-370.78, 0) * mm});
            skLineSegment(sketch, "E115", {"start": v(-370.78, 0) * mm, "end": v(-512.37, 0) * mm});
            skLineSegment(sketch, "E116", {"start": v(-512.37, 0) * mm, "end": v(-522.13, 7.94) * mm});
            skLineSegment(sketch, "E117", {"start": v(370.73, 0) * mm, "end": v(382.25, 7.94) * mm});
            skLineSegment(sketch, "E118", {"start": v(382.25, 7.94) * mm, "end": v(522.25, 7.94) * mm});
            skLineSegment(sketch, "E119", {"start": v(522.25, 7.94) * mm, "end": v(512.32, 0) * mm});
            skLineSegment(sketch, "E120", {"start": v(512.32, 0) * mm, "end": v(370.73, 0) * mm});
            skSolve(sketch);
        }
        {
            var Q0;
            Q0 = qSketchRegion(id + "F34", true);
            extrude(context, id + "F35", {"entities" : qUnion([Q0]), "depth" : 4.6 * mm});
        }
        {
            var Q0;
            Q0=makeQuery(id+"F1.opExtrude","SWEPT_FACE",FACE,{"disambiguationData":[OSD([sQuery(id+"F0.wireOp",EDGE,"E7")])]});
            var sketch = newSketch(context, id + "F36", { "sketchPlane" : qUnion([Q0])});
            skLineSegment(sketch, "E121", {"start": v(-6950.08, -80) * mm, "end": v(-6709.7, -504.23) * mm});
            skLineSegment(sketch, "E122", {"start": v(-6699.7, -504.23) * mm, "end": v(-6940.08, -80) * mm});
            skLineSegment(sketch, "E123", {"start": v(-6940.08, -80) * mm, "end": v(-6950.08, -80) * mm});
            skLineSegment(sketch, "E124", {"start": v(-6709.7, -504.23) * mm, "end": v(-6699.7, -504.23) * mm});
            skSolve(sketch);
        }
        {
            var Q0;
            Q0 = qSketchRegion(id + "F36", true);
            extrude(context, id + "F37", {"entities" : qUnion([Q0]), "endBound" : BoundingType.UP_TO_NEXT, "depth" : 25 * mm});
        }
        {
            var Q0;
            Q0=makeQuery(id+"F18.opExtrude","SWEPT_FACE",FACE,{"disambiguationData":[OSD([sQuery(id+"F17.wireOp",EDGE,"E37.top")])]});
            var sketch = newSketch(context, id + "F38", { "sketchPlane" : qUnion([Q0])});
            skLineSegment(sketch, "E125.bottom", {"start": v(-421.1, -6930) * mm, "end": v(438.57, -6930) * mm});
            skLineSegment(sketch, "E125.top", {"start": v(-421.1, -6711.58) * mm, "end": v(438.57, -6711.58) * mm});
            skLineSegment(sketch, "E125.left", {"start": v(-421.1, -6930) * mm, "end": v(-421.1, -6711.58) * mm});
            skLineSegment(sketch, "E125.right", {"start": v(438.57, -6930) * mm, "end": v(438.57, -6711.58) * mm});
            skSolve(sketch);
        }
        {
            var Q0;
            Q0 = qSketchRegion(id + "F38", true);
            extrude(context, id + "F39", {"entities" : qUnion([Q0]), "operationType" : NewBodyOperationType.REMOVE, "oppositeDirection" : true, "depth" : 25 * mm});
        }
        {
            var Q0;
            Q0=makeQuery(id+"F1.opExtrude","SWEPT_FACE",FACE,{"disambiguationData":[OSD([sQuery(id+"F0.wireOp",EDGE,"E10.2")])]});
            var sketch = newSketch(context, id + "F40", { "sketchPlane" : qUnion([Q0])});
            skLineSegment(sketch, "E126.bottom", {"start": v(50, 1759.48) * mm, "end": v(6500, 1759.48) * mm});
            skLineSegment(sketch, "E126.top", {"start": v(50, 36.75) * mm, "end": v(6500, 36.75) * mm});
            skLineSegment(sketch, "E126.left", {"start": v(50, 1759.48) * mm, "end": v(50, 36.75) * mm});
            skLineSegment(sketch, "E126.right", {"start": v(6500, 1759.48) * mm, "end": v(6500, 36.75) * mm});
            skLineSegment(sketch, "E127.0", {"start": v(30, 1779.48) * mm, "end": v(6520, 1779.48) * mm});
            skLineSegment(sketch, "E127.1", {"start": v(30, 1779.48) * mm, "end": v(30, 16.75) * mm});
            skLineSegment(sketch, "E127.2", {"start": v(30, 16.75) * mm, "end": v(6520, 16.75) * mm});
            skLineSegment(sketch, "E127.3", {"start": v(6520, 1779.48) * mm, "end": v(6520, 16.75) * mm});
            skSolve(sketch);
        }
        {
            var Q0;
            Q0 = qSketchRegion(id + "F40", true);
            extrude(context, id + "F41", {"entities" : qUnion([Q0]), "depth" : 1 * mm});
        }
        {
            var Q0;
            Q0=makeQuery(id+"F1.opExtrude","SWEPT_FACE",FACE,{"disambiguationData":[OSD([sQuery(id+"F0.wireOp",EDGE,"E10.7")])]});
            var sketch = newSketch(context, id + "F42", { "sketchPlane" : qUnion([Q0])});
            skLineSegment(sketch, "E128", {"start": v(-6500, 1759.48) * mm, "end": v(-50, 1759.48) * mm});
            skLineSegment(sketch, "E129", {"start": v(-50, 1759.48) * mm, "end": v(-50, 1414.22) * mm});
            skLineSegment(sketch, "E130", {"start": v(-50, 1414.22) * mm, "end": v(-480.24, 1159.48) * mm});
            skLineSegment(sketch, "E131", {"start": v(-480.24, 1159.48) * mm, "end": v(-6500, 1159.48) * mm});
            skLineSegment(sketch, "E132", {"start": v(-6500, 1159.48) * mm, "end": v(-6500, 1759.48) * mm});
            skLineSegment(sketch, "E133.0", {"start": v(-30, 1779.48) * mm, "end": v(-30, 1402.82) * mm});
            skLineSegment(sketch, "E133.1", {"start": v(-6520, 1779.48) * mm, "end": v(-30, 1779.48) * mm});
            skLineSegment(sketch, "E133.2", {"start": v(-30, 1402.82) * mm, "end": v(-474.77, 1139.48) * mm});
            skLineSegment(sketch, "E133.3", {"start": v(-474.77, 1139.48) * mm, "end": v(-6520, 1139.48) * mm});
            skLineSegment(sketch, "E133.4", {"start": v(-6520, 1139.48) * mm, "end": v(-6520, 1779.48) * mm});
            skSolve(sketch);
        }
        {
            var Q0;
            Q0 = qSketchRegion(id + "F42", true);
            extrude(context, id + "F43", {"entities" : qUnion([Q0]), "depth" : 1 * mm});
        }
        {
            var Q0;
            Q0=makeQuery(id+"F1.opExtrude","SWEPT_FACE",FACE,{"disambiguationData":[OSD([sQuery(id+"F0.wireOp",EDGE,"E10.2")])]});
            var sketch = newSketch(context, id + "F44", { "sketchPlane" : qUnion([Q0])});
            skCircle(sketch, "E134", {"center": v(450, -423.25) * mm, "radius": 325 * mm});
            skCircle(sketch, "E135", {"center": v(450, -423.25) * mm, "radius": 250 * mm});
            skCircle(sketch, "E136", {"center": v(6500, -423.25) * mm, "radius": 325 * mm});
            skCircle(sketch, "E137", {"center": v(6500, -423.25) * mm, "radius": 250 * mm});
            skSolve(sketch);
        }
        {
            var Q0;
            Q0 = qSketchRegion(id + "F44", true);
            extrude(context, id + "F45", {"entities" : qUnion([Q0]), "endBound" : BoundingType.SYMMETRIC, "depth" : 200 * mm});
        }
        {
            var Q0;
            Q0=makeQuery(id+"F45.opExtrude","CAP_EDGE",EDGE,{"disambiguationData":[OSD([sQuery(id+"F44.wireOp",EDGE,"E136")])],"isStart":false});
            var Q1;
            Q1=makeQuery(id+"F45.opExtrude","CAP_EDGE",EDGE,{"disambiguationData":[OSD([sQuery(id+"F44.wireOp",EDGE,"E136")])],"isStart":true});
            var Q2;
            Q2=makeQuery(id+"F45.opExtrude","CAP_EDGE",EDGE,{"disambiguationData":[OSD([sQuery(id+"F44.wireOp",EDGE,"E134")])],"isStart":false});
            var Q3;
            Q3=makeQuery(id+"F45.opExtrude","CAP_EDGE",EDGE,{"disambiguationData":[OSD([sQuery(id+"F44.wireOp",EDGE,"E134")])],"isStart":true});
            fillet(context, id + "F46", {"entities" : qUnion([Q0, Q1, Q2, Q3]), "radius" : 20 * mm, "tangentPropagation" : true, "allowEdgeOverflow" : false});
        }
        {
            var Q0;
            Q0=makeQuery(id+"F45.opExtrude","CAP_EDGE",EDGE,{"disambiguationData":[OSD([sQuery(id+"F44.wireOp",EDGE,"E135")])],"isStart":false});
            var Q1;
            Q1=makeQuery(id+"F45.opExtrude","CAP_EDGE",EDGE,{"disambiguationData":[OSD([sQuery(id+"F44.wireOp",EDGE,"E135")])],"isStart":true});
            var Q2;
            Q2=makeQuery(id+"F45.opExtrude","CAP_EDGE",EDGE,{"disambiguationData":[OSD([sQuery(id+"F44.wireOp",EDGE,"E137")])],"isStart":true});
            var Q3;
            Q3=makeQuery(id+"F45.opExtrude","CAP_EDGE",EDGE,{"disambiguationData":[OSD([sQuery(id+"F44.wireOp",EDGE,"E137")])],"isStart":false});
            fillet(context, id + "F47", {"entities" : qUnion([Q0, Q1, Q2, Q3]), "radius" : 5 * mm, "tangentPropagation" : true, "allowEdgeOverflow" : false});
        }
        {
            var Q0;
            Q0=makeQuery(id+"F1.opExtrude","SWEPT_FACE",FACE,{"disambiguationData":[OSD([sQuery(id+"F0.wireOp",EDGE,"E10.2")])]});
            var sketch = newSketch(context, id + "F48", { "sketchPlane" : qUnion([Q0])});
            skSolve(sketch);
        }
        {
            var Q0;
            Q0=makeQuery(id+"F45.opExtrude","CAP_FACE",FACE,{"disambiguationData":[OSD([sQuery(id+"F44.wireOp",EDGE,"E134"),sQuery(id+"F44.wireOp",EDGE,"E135")])],"isStart":false});
            var sketch = newSketch(context, id + "F49", { "sketchPlane" : qUnion([Q0])});
            skCircle(sketch, "E138", {"center": v(450, -423.25) * mm, "radius": 250 * mm});
            skArc(sketch, "E139", {"start": v(400, -229.6) * mm, "mid": v(308.58, -281.83) * mm, "end": v(256.35, -373.25) * mm});
            skCircle(sketch, "E140", {"center": v(6500, -423.25) * mm, "radius": 250 * mm});
            skArc(sketch, "E141", {"start": v(6450, -229.6) * mm, "mid": v(6358.58, -281.83) * mm, "end": v(6306.35, -373.25) * mm});
            skArc(sketch, "E142", {"start": v(400, -308.68) * mm, "mid": v(361.61, -334.86) * mm, "end": v(335.44, -373.25) * mm});
            skLineSegment(sketch, "E143.rect.left", {"start": v(500, -229.6) * mm, "end": v(500, -308.68) * mm});
            skLineSegment(sketch, "E143.rect.right", {"start": v(400, -229.6) * mm, "end": v(400, -308.68) * mm});
            skLineSegment(sketch, "E144.rect.bottom", {"start": v(643.65, -373.25) * mm, "end": v(564.56, -373.25) * mm});
            skLineSegment(sketch, "E144.rect.top", {"start": v(643.65, -473.25) * mm, "end": v(564.56, -473.25) * mm});
            skArc(sketch, "E145", {"start": v(6450, -308.68) * mm, "mid": v(6411.61, -334.86) * mm, "end": v(6385.44, -373.25) * mm});
            skLineSegment(sketch, "E146.rect.left", {"start": v(6550, -229.6) * mm, "end": v(6550, -308.68) * mm});
            skLineSegment(sketch, "E146.rect.right", {"start": v(6450, -229.6) * mm, "end": v(6450, -308.68) * mm});
            skLineSegment(sketch, "E147.rect.bottom", {"start": v(6693.65, -473.25) * mm, "end": v(6614.56, -473.25) * mm});
            skLineSegment(sketch, "E147.rect.top", {"start": v(6693.65, -373.25) * mm, "end": v(6614.56, -373.25) * mm});
            skPoint(sketch, "E148.orphan", {"position": v(400, -206.91) * mm});
            skPoint(sketch, "E149.orphan", {"position": v(500, -206.91) * mm});
            skLineSegment(sketch, "E150.trimOffspring", {"start": v(400, -537.81) * mm, "end": v(400, -616.9) * mm});
            skLineSegment(sketch, "E151.trimOffspring", {"start": v(500, -537.81) * mm, "end": v(500, -616.9) * mm});
            skArc(sketch, "E152.trimOffspring", {"start": v(564.56, -373.25) * mm, "mid": v(538.39, -334.86) * mm, "end": v(500, -308.68) * mm});
            skArc(sketch, "E153.trimOffspring", {"start": v(643.65, -373.25) * mm, "mid": v(591.42, -281.83) * mm, "end": v(500, -229.6) * mm});
            skLineSegment(sketch, "E154.trimOffspring", {"start": v(335.44, -473.25) * mm, "end": v(256.35, -473.25) * mm});
            skArc(sketch, "E155.trimOffspring", {"start": v(500, -537.81) * mm, "mid": v(538.39, -511.64) * mm, "end": v(564.56, -473.25) * mm});
            skArc(sketch, "E156.trimOffspring", {"start": v(500, -616.9) * mm, "mid": v(591.42, -564.67) * mm, "end": v(643.65, -473.25) * mm});
            skPoint(sketch, "E157.orphan", {"position": v(400, -639.59) * mm});
            skPoint(sketch, "E158.orphan", {"position": v(500, -639.59) * mm});
            skPoint(sketch, "E159.orphan", {"position": v(235.67, -373.25) * mm});
            skPoint(sketch, "E160.orphan", {"position": v(235.67, -473.25) * mm});
            skArc(sketch, "E161.trimOffspring", {"start": v(256.35, -473.25) * mm, "mid": v(308.58, -564.67) * mm, "end": v(400, -616.9) * mm});
            skArc(sketch, "E162.trimOffspring", {"start": v(335.44, -473.25) * mm, "mid": v(361.61, -511.64) * mm, "end": v(400, -537.81) * mm});
            skLineSegment(sketch, "E163.trimOffspring", {"start": v(335.44, -373.25) * mm, "end": v(256.35, -373.25) * mm});
            skPoint(sketch, "E164.orphan", {"position": v(664.33, -373.25) * mm});
            skPoint(sketch, "E165.orphan", {"position": v(664.33, -473.25) * mm});
            skPoint(sketch, "E166.orphan", {"position": v(6550, -196.6) * mm});
            skPoint(sketch, "E167.orphan", {"position": v(6450, -196.6) * mm});
            skLineSegment(sketch, "E168.trimOffspring", {"start": v(6450, -537.81) * mm, "end": v(6450, -616.9) * mm});
            skLineSegment(sketch, "E169.trimOffspring", {"start": v(6385.44, -373.25) * mm, "end": v(6306.35, -373.25) * mm});
            skLineSegment(sketch, "E170.trimOffspring", {"start": v(6550, -537.81) * mm, "end": v(6550, -616.9) * mm});
            skArc(sketch, "E171.trimOffspring", {"start": v(6306.35, -473.25) * mm, "mid": v(6358.58, -564.67) * mm, "end": v(6450, -616.9) * mm});
            skArc(sketch, "E172.trimOffspring", {"start": v(6385.44, -473.25) * mm, "mid": v(6411.61, -511.64) * mm, "end": v(6450, -537.81) * mm});
            skPoint(sketch, "E173.orphan", {"position": v(6280.22, -373.25) * mm});
            skPoint(sketch, "E174.orphan", {"position": v(6280.22, -473.25) * mm});
            skLineSegment(sketch, "E175.trimOffspring", {"start": v(6385.44, -473.25) * mm, "end": v(6306.35, -473.25) * mm});
            skArc(sketch, "E176.trimOffspring", {"start": v(6614.56, -373.25) * mm, "mid": v(6588.39, -334.86) * mm, "end": v(6550, -308.68) * mm});
            skArc(sketch, "E177.trimOffspring", {"start": v(6693.65, -373.25) * mm, "mid": v(6641.42, -281.83) * mm, "end": v(6550, -229.6) * mm});
            skPoint(sketch, "E178.orphan", {"position": v(6719.78, -373.25) * mm});
            skPoint(sketch, "E179.orphan", {"position": v(6719.78, -473.25) * mm});
            skArc(sketch, "E180.trimOffspring", {"start": v(6550, -537.81) * mm, "mid": v(6588.39, -511.64) * mm, "end": v(6614.56, -473.25) * mm});
            skArc(sketch, "E181.trimOffspring", {"start": v(6550, -616.9) * mm, "mid": v(6641.42, -564.67) * mm, "end": v(6693.65, -473.25) * mm});
            skPoint(sketch, "E146.rect.top.end.orphan", {"position": v(6450, -649.9) * mm});
            skPoint(sketch, "E146.rect.top.start.orphan", {"position": v(6550, -649.9) * mm});
            skSolve(sketch);
        }
        {
            var Q0;
            Q0 = qSketchRegion(id + "F49", true);
            extrude(context, id + "F50", {"entities" : qUnion([Q0]), "oppositeDirection" : true, "depth" : 20 * mm});
        }
        {
            var Q0;
            Q0=makeQuery(id+"F50.opExtrude","CAP_EDGE",EDGE,{"disambiguationData":[OSD([sQuery(id+"F49.wireOp",EDGE,"E139")])],"isStart":true});
            var Q1;
            Q1=makeQuery(id+"F50.opExtrude","CAP_EDGE",EDGE,{"disambiguationData":[OSD([sQuery(id+"F49.wireOp",EDGE,"E163.trimOffspring")])],"isStart":true});
            var Q2;
            Q2=makeQuery(id+"F50.opExtrude","CAP_EDGE",EDGE,{"disambiguationData":[OSD([sQuery(id+"F49.wireOp",EDGE,"E142")])],"isStart":true});
            var Q3;
            Q3=makeQuery(id+"F50.opExtrude","CAP_EDGE",EDGE,{"disambiguationData":[OSD([sQuery(id+"F49.wireOp",EDGE,"E143.rect.right")])],"isStart":true});
            var Q4;
            Q4=makeQuery(id+"F50.opExtrude","CAP_EDGE",EDGE,{"disambiguationData":[OSD([sQuery(id+"F49.wireOp",EDGE,"E153.trimOffspring")])],"isStart":true});
            var Q5;
            Q5=makeQuery(id+"F50.opExtrude","CAP_EDGE",EDGE,{"disambiguationData":[OSD([sQuery(id+"F49.wireOp",EDGE,"E143.rect.left")])],"isStart":true});
            var Q6;
            Q6=makeQuery(id+"F50.opExtrude","CAP_EDGE",EDGE,{"disambiguationData":[OSD([sQuery(id+"F49.wireOp",EDGE,"E152.trimOffspring")])],"isStart":true});
            var Q7;
            Q7=makeQuery(id+"F50.opExtrude","CAP_EDGE",EDGE,{"disambiguationData":[OSD([sQuery(id+"F49.wireOp",EDGE,"E144.rect.bottom")])],"isStart":true});
            var Q8;
            Q8=makeQuery(id+"F50.opExtrude","CAP_EDGE",EDGE,{"disambiguationData":[OSD([sQuery(id+"F49.wireOp",EDGE,"E155.trimOffspring")])],"isStart":true});
            var Q9;
            Q9=makeQuery(id+"F50.opExtrude","CAP_EDGE",EDGE,{"disambiguationData":[OSD([sQuery(id+"F49.wireOp",EDGE,"E144.rect.top")])],"isStart":true});
            var Q10;
            Q10=makeQuery(id+"F50.opExtrude","CAP_EDGE",EDGE,{"disambiguationData":[OSD([sQuery(id+"F49.wireOp",EDGE,"E156.trimOffspring")])],"isStart":true});
            var Q11;
            Q11=makeQuery(id+"F50.opExtrude","CAP_EDGE",EDGE,{"disambiguationData":[OSD([sQuery(id+"F49.wireOp",EDGE,"E151.trimOffspring")])],"isStart":true});
            var Q12;
            Q12=makeQuery(id+"F50.opExtrude","CAP_EDGE",EDGE,{"disambiguationData":[OSD([sQuery(id+"F49.wireOp",EDGE,"E150.trimOffspring")])],"isStart":true});
            var Q13;
            Q13=makeQuery(id+"F50.opExtrude","CAP_EDGE",EDGE,{"disambiguationData":[OSD([sQuery(id+"F49.wireOp",EDGE,"E162.trimOffspring")])],"isStart":true});
            var Q14;
            Q14=makeQuery(id+"F50.opExtrude","CAP_EDGE",EDGE,{"disambiguationData":[OSD([sQuery(id+"F49.wireOp",EDGE,"E154.trimOffspring")])],"isStart":true});
            var Q15;
            Q15=makeQuery(id+"F50.opExtrude","CAP_EDGE",EDGE,{"disambiguationData":[OSD([sQuery(id+"F49.wireOp",EDGE,"E161.trimOffspring")])],"isStart":true});
            fillet(context, id + "F51", {"entities" : qUnion([Q0, Q1, Q2, Q3, Q4, Q5, Q6, Q7, Q8, Q9, Q10, Q11, Q12, Q13, Q14, Q15]), "radius" : 50 * mm, "tangentPropagation" : true, "allowEdgeOverflow" : false});
        }
        {
            var Q0;
            Q0=makeQuery(id+"F50.opExtrude","CAP_FACE",FACE,{"disambiguationData":[OSD([sQuery(id+"F49.wireOp",EDGE,"E140"),sQuery(id+"F49.wireOp",EDGE,"E141"),sQuery(id+"F49.wireOp",EDGE,"E145"),sQuery(id+"F49.wireOp",EDGE,"E146.rect.left"),sQuery(id+"F49.wireOp",EDGE,"E146.rect.right"),sQuery(id+"F49.wireOp",EDGE,"E147.rect.bottom"),sQuery(id+"F49.wireOp",EDGE,"E147.rect.top"),sQuery(id+"F49.wireOp",EDGE,"E168.trimOffspring"),sQuery(id+"F49.wireOp",EDGE,"E169.trimOffspring"),sQuery(id+"F49.wireOp",EDGE,"E170.trimOffspring"),sQuery(id+"F49.wireOp",EDGE,"E171.trimOffspring"),sQuery(id+"F49.wireOp",EDGE,"E172.trimOffspring"),sQuery(id+"F49.wireOp",EDGE,"E175.trimOffspring"),sQuery(id+"F49.wireOp",EDGE,"E176.trimOffspring"),sQuery(id+"F49.wireOp",EDGE,"E177.trimOffspring"),sQuery(id+"F49.wireOp",EDGE,"E180.trimOffspring"),sQuery(id+"F49.wireOp",EDGE,"E181.trimOffspring")])],"isStart":true});
            var Q1;
            Q1=makeQuery(id+"F50.opExtrude","CAP_EDGE",EDGE,{"disambiguationData":[OSD([sQuery(id+"F49.wireOp",EDGE,"E145")])],"isStart":true});
            var Q2;
            Q2=makeQuery(id+"F50.opExtrude","CAP_EDGE",EDGE,{"disambiguationData":[OSD([sQuery(id+"F49.wireOp",EDGE,"E141")])],"isStart":true});
            var Q3;
            Q3=makeQuery(id+"F50.opExtrude","CAP_EDGE",EDGE,{"disambiguationData":[OSD([sQuery(id+"F49.wireOp",EDGE,"E146.rect.right")])],"isStart":true});
            var Q4;
            Q4=makeQuery(id+"F50.opExtrude","CAP_EDGE",EDGE,{"disambiguationData":[OSD([sQuery(id+"F49.wireOp",EDGE,"E169.trimOffspring")])],"isStart":true});
            var Q5;
            Q5=makeQuery(id+"F50.opExtrude","CAP_EDGE",EDGE,{"disambiguationData":[OSD([sQuery(id+"F49.wireOp",EDGE,"E146.rect.left")])],"isStart":true});
            var Q6;
            Q6=makeQuery(id+"F50.opExtrude","CAP_EDGE",EDGE,{"disambiguationData":[OSD([sQuery(id+"F49.wireOp",EDGE,"E177.trimOffspring")])],"isStart":true});
            var Q7;
            Q7=makeQuery(id+"F50.opExtrude","CAP_EDGE",EDGE,{"disambiguationData":[OSD([sQuery(id+"F49.wireOp",EDGE,"E176.trimOffspring")])],"isStart":true});
            var Q8;
            Q8=makeQuery(id+"F50.opExtrude","CAP_EDGE",EDGE,{"disambiguationData":[OSD([sQuery(id+"F49.wireOp",EDGE,"E147.rect.top")])],"isStart":true});
            var Q9;
            Q9=makeQuery(id+"F50.opExtrude","CAP_EDGE",EDGE,{"disambiguationData":[OSD([sQuery(id+"F49.wireOp",EDGE,"E180.trimOffspring")])],"isStart":true});
            var Q10;
            Q10=makeQuery(id+"F50.opExtrude","CAP_EDGE",EDGE,{"disambiguationData":[OSD([sQuery(id+"F49.wireOp",EDGE,"E181.trimOffspring")])],"isStart":true});
            var Q11;
            Q11=makeQuery(id+"F50.opExtrude","CAP_EDGE",EDGE,{"disambiguationData":[OSD([sQuery(id+"F49.wireOp",EDGE,"E170.trimOffspring")])],"isStart":true});
            var Q12;
            Q12=makeQuery(id+"F50.opExtrude","CAP_EDGE",EDGE,{"disambiguationData":[OSD([sQuery(id+"F49.wireOp",EDGE,"E147.rect.bottom")])],"isStart":true});
            var Q13;
            Q13=makeQuery(id+"F50.opExtrude","CAP_EDGE",EDGE,{"disambiguationData":[OSD([sQuery(id+"F49.wireOp",EDGE,"E168.trimOffspring")])],"isStart":true});
            fillet(context, id + "F52", {"entities" : qUnion([Q0, Q1, Q2, Q3, Q4, Q5, Q6, Q7, Q8, Q9, Q10, Q11, Q12, Q13]), "radius" : 60 * mm, "tangentPropagation" : true, "allowEdgeOverflow" : false});
        }
        {
            var Q0;
            Q0=makeQuery(id+"F1.opExtrude","SWEPT_FACE",FACE,{"disambiguationData":[OSD([sQuery(id+"F0.wireOp",EDGE,"E10.7")])]});
            var sketch = newSketch(context, id + "F53", { "sketchPlane" : qUnion([Q0])});
            skCircle(sketch, "E182", {"center": v(-6500, -422.74) * mm, "radius": 325 * mm});
            skCircle(sketch, "E183", {"center": v(-6500, -422.74) * mm, "radius": 250 * mm});
            skCircle(sketch, "E184", {"center": v(-450, -422.74) * mm, "radius": 325 * mm});
            skCircle(sketch, "E185", {"center": v(-450, -422.74) * mm, "radius": 250 * mm});
            skSolve(sketch);
        }
        {
            var Q0;
            Q0 = qSketchRegion(id + "F53", true);
            extrude(context, id + "F54", {"entities" : qUnion([Q0]), "endBound" : BoundingType.SYMMETRIC, "depth" : 200 * mm});
        }
        {
            var Q0;
            Q0=makeQuery(id+"F54.opExtrude","CAP_EDGE",EDGE,{"disambiguationData":[OSD([sQuery(id+"F53.wireOp",EDGE,"E184")])],"isStart":false});
            var Q1;
            Q1=makeQuery(id+"F54.opExtrude","CAP_EDGE",EDGE,{"disambiguationData":[OSD([sQuery(id+"F53.wireOp",EDGE,"E182")])],"isStart":false});
            fillet(context, id + "F55", {"entities" : qUnion([Q0, Q1]), "radius" : 20 * mm, "tangentPropagation" : true, "allowEdgeOverflow" : false});
        }
        {
            var Q0;
            Q0=makeQuery(id+"F54.opExtrude","CAP_EDGE",EDGE,{"disambiguationData":[OSD([sQuery(id+"F53.wireOp",EDGE,"E184")])],"isStart":true});
            var Q1;
            Q1=makeQuery(id+"F54.opExtrude","CAP_EDGE",EDGE,{"disambiguationData":[OSD([sQuery(id+"F53.wireOp",EDGE,"E182")])],"isStart":true});
            fillet(context, id + "F56", {"entities" : qUnion([Q0, Q1]), "radius" : 20 * mm, "tangentPropagation" : true, "allowEdgeOverflow" : false});
        }
        {
            var Q0;
            Q0=makeQuery(id+"F54.opExtrude","CAP_EDGE",EDGE,{"disambiguationData":[OSD([sQuery(id+"F53.wireOp",EDGE,"E183")])],"isStart":true});
            var Q1;
            Q1=makeQuery(id+"F54.opExtrude","CAP_EDGE",EDGE,{"disambiguationData":[OSD([sQuery(id+"F53.wireOp",EDGE,"E183")])],"isStart":false});
            var Q2;
            Q2=makeQuery(id+"F54.opExtrude","CAP_EDGE",EDGE,{"disambiguationData":[OSD([sQuery(id+"F53.wireOp",EDGE,"E185")])],"isStart":true});
            var Q3;
            Q3=makeQuery(id+"F54.opExtrude","CAP_EDGE",EDGE,{"disambiguationData":[OSD([sQuery(id+"F53.wireOp",EDGE,"E185")])],"isStart":false});
            fillet(context, id + "F57", {"entities" : qUnion([Q0, Q1, Q2, Q3]), "radius" : 5 * mm, "tangentPropagation" : true, "allowEdgeOverflow" : false});
        }
        {
            var Q0;
            Q0=makeQuery(id+"F54.opExtrude","CAP_FACE",FACE,{"disambiguationData":[OSD([sQuery(id+"F53.wireOp",EDGE,"E182"),sQuery(id+"F53.wireOp",EDGE,"E183")])],"isStart":false});
            var sketch = newSketch(context, id + "F58", { "sketchPlane" : qUnion([Q0])});
            skCircle(sketch, "E186", {"center": v(-6500, -422.74) * mm, "radius": 250 * mm});
            skCircle(sketch, "E187", {"center": v(-450, -422.74) * mm, "radius": 250 * mm});
            skArc(sketch, "E188", {"start": v(-643.65, -472.74) * mm, "mid": v(-591.42, -564.16) * mm, "end": v(-500, -616.39) * mm});
            skArc(sketch, "E189", {"start": v(-6693.65, -472.74) * mm, "mid": v(-6641.42, -564.16) * mm, "end": v(-6550, -616.39) * mm});
            skArc(sketch, "E190", {"start": v(-6614.56, -472.74) * mm, "mid": v(-6588.39, -511.13) * mm, "end": v(-6550, -537.3) * mm});
            skArc(sketch, "E191", {"start": v(-564.56, -472.74) * mm, "mid": v(-538.39, -511.13) * mm, "end": v(-500, -537.3) * mm});
            skLineSegment(sketch, "E192.rect.left", {"start": v(-6450, -616.39) * mm, "end": v(-6450, -537.3) * mm});
            skLineSegment(sketch, "E192.rect.right", {"start": v(-6550, -616.39) * mm, "end": v(-6550, -537.3) * mm});
            skLineSegment(sketch, "E193.rect.bottom", {"start": v(-6306.35, -472.74) * mm, "end": v(-6385.44, -472.74) * mm});
            skLineSegment(sketch, "E193.rect.top", {"start": v(-6306.35, -372.74) * mm, "end": v(-6385.44, -372.74) * mm});
            skLineSegment(sketch, "E194.rect.bottom", {"start": v(-643.65, -372.74) * mm, "end": v(-564.56, -372.74) * mm});
            skLineSegment(sketch, "E194.rect.top", {"start": v(-643.65, -472.74) * mm, "end": v(-564.56, -472.74) * mm});
            skLineSegment(sketch, "E195.rect.left", {"start": v(-500, -229.09) * mm, "end": v(-500, -308.17) * mm});
            skLineSegment(sketch, "E195.rect.right", {"start": v(-400, -229.09) * mm, "end": v(-400, -308.17) * mm});
            skLineSegment(sketch, "E196.trimOffspring", {"start": v(-6550, -308.17) * mm, "end": v(-6550, -229.09) * mm});
            skLineSegment(sketch, "E197.trimOffspring", {"start": v(-6450, -308.17) * mm, "end": v(-6450, -229.09) * mm});
            skArc(sketch, "E198.trimOffspring", {"start": v(-6385.44, -372.74) * mm, "mid": v(-6411.61, -334.35) * mm, "end": v(-6450, -308.17) * mm});
            skArc(sketch, "E199.trimOffspring", {"start": v(-6306.35, -372.74) * mm, "mid": v(-6358.58, -281.32) * mm, "end": v(-6450, -229.09) * mm});
            skPoint(sketch, "E200.orphan", {"position": v(-6281.42, -372.74) * mm});
            skPoint(sketch, "E201.orphan", {"position": v(-6281.42, -472.74) * mm});
            skPoint(sketch, "E202.orphan", {"position": v(-6718.58, -472.74) * mm});
            skPoint(sketch, "E203.orphan", {"position": v(-6718.58, -372.74) * mm});
            skLineSegment(sketch, "E204.trimOffspring", {"start": v(-6614.56, -372.74) * mm, "end": v(-6693.65, -372.74) * mm});
            skLineSegment(sketch, "E205.trimOffspring", {"start": v(-6614.56, -472.74) * mm, "end": v(-6693.65, -472.74) * mm});
            skArc(sketch, "E206.trimOffspring", {"start": v(-6550, -229.09) * mm, "mid": v(-6641.42, -281.32) * mm, "end": v(-6693.65, -372.74) * mm});
            skArc(sketch, "E207.trimOffspring", {"start": v(-6550, -308.17) * mm, "mid": v(-6588.39, -334.35) * mm, "end": v(-6614.56, -372.74) * mm});
            skArc(sketch, "E208.trimOffspring", {"start": v(-6450, -537.3) * mm, "mid": v(-6411.61, -511.13) * mm, "end": v(-6385.44, -472.74) * mm});
            skArc(sketch, "E209.trimOffspring", {"start": v(-6450, -616.39) * mm, "mid": v(-6358.58, -564.16) * mm, "end": v(-6306.35, -472.74) * mm});
            skPoint(sketch, "E210.orphan", {"position": v(-6550, -202.77) * mm});
            skPoint(sketch, "E211.orphan", {"position": v(-6550, -642.7) * mm});
            skPoint(sketch, "E212.orphan", {"position": v(-6450, -642.7) * mm});
            skPoint(sketch, "E213.orphan", {"position": v(-6450, -202.77) * mm});
            skLineSegment(sketch, "E214.trimOffspring", {"start": v(-500, -537.3) * mm, "end": v(-500, -616.39) * mm});
            skLineSegment(sketch, "E215.trimOffspring", {"start": v(-400, -537.3) * mm, "end": v(-400, -616.39) * mm});
            skArc(sketch, "E216.trimOffspring", {"start": v(-335.44, -372.74) * mm, "mid": v(-361.61, -334.35) * mm, "end": v(-400, -308.17) * mm});
            skArc(sketch, "E217.trimOffspring", {"start": v(-256.35, -372.74) * mm, "mid": v(-308.58, -281.32) * mm, "end": v(-400, -229.09) * mm});
            skArc(sketch, "E218.trimOffspring", {"start": v(-500, -229.09) * mm, "mid": v(-591.42, -281.32) * mm, "end": v(-643.65, -372.74) * mm});
            skArc(sketch, "E219.trimOffspring", {"start": v(-500, -308.17) * mm, "mid": v(-538.39, -334.35) * mm, "end": v(-564.56, -372.74) * mm});
            skLineSegment(sketch, "E220.trimOffspring", {"start": v(-335.44, -372.74) * mm, "end": v(-256.35, -372.74) * mm});
            skLineSegment(sketch, "E221.trimOffspring", {"start": v(-335.44, -472.74) * mm, "end": v(-256.35, -472.74) * mm});
            skArc(sketch, "E222.trimOffspring", {"start": v(-400, -537.3) * mm, "mid": v(-361.61, -511.13) * mm, "end": v(-335.44, -472.74) * mm});
            skArc(sketch, "E223.trimOffspring", {"start": v(-400, -616.39) * mm, "mid": v(-308.58, -564.16) * mm, "end": v(-256.35, -472.74) * mm});
            skPoint(sketch, "E224.orphan", {"position": v(-222.23, -372.74) * mm});
            skPoint(sketch, "E225.orphan", {"position": v(-222.23, -472.74) * mm});
            skPoint(sketch, "E226.orphan", {"position": v(-677.77, -372.74) * mm});
            skPoint(sketch, "E227.orphan", {"position": v(-677.77, -472.74) * mm});
            skPoint(sketch, "E228.orphan", {"position": v(-500, -638.49) * mm});
            skPoint(sketch, "E229.orphan", {"position": v(-500, -206.99) * mm});
            skPoint(sketch, "E230.orphan", {"position": v(-400, -206.99) * mm});
            skPoint(sketch, "E231.orphan", {"position": v(-400, -638.49) * mm});
            skSolve(sketch);
        }
        {
            var Q0;
            Q0 = qSketchRegion(id + "F58", true);
            extrude(context, id + "F59", {"entities" : qUnion([Q0]), "oppositeDirection" : true, "depth" : 20 * mm});
        }
        {
            var Q0;
            Q0=makeQuery(id+"F59.opExtrude","CAP_EDGE",EDGE,{"disambiguationData":[OSD([sQuery(id+"F58.wireOp",EDGE,"E218.trimOffspring")])],"isStart":true});
            var Q1;
            Q1=makeQuery(id+"F59.opExtrude","CAP_EDGE",EDGE,{"disambiguationData":[OSD([sQuery(id+"F58.wireOp",EDGE,"E195.rect.left")])],"isStart":true});
            var Q2;
            Q2=makeQuery(id+"F59.opExtrude","CAP_EDGE",EDGE,{"disambiguationData":[OSD([sQuery(id+"F58.wireOp",EDGE,"E219.trimOffspring")])],"isStart":true});
            var Q3;
            Q3=makeQuery(id+"F59.opExtrude","CAP_EDGE",EDGE,{"disambiguationData":[OSD([sQuery(id+"F58.wireOp",EDGE,"E194.rect.bottom")])],"isStart":true});
            var Q4;
            Q4=makeQuery(id+"F59.opExtrude","CAP_EDGE",EDGE,{"disambiguationData":[OSD([sQuery(id+"F58.wireOp",EDGE,"E195.rect.right")])],"isStart":true});
            var Q5;
            Q5=makeQuery(id+"F59.opExtrude","CAP_EDGE",EDGE,{"disambiguationData":[OSD([sQuery(id+"F58.wireOp",EDGE,"E217.trimOffspring")])],"isStart":true});
            var Q6;
            Q6=makeQuery(id+"F59.opExtrude","CAP_EDGE",EDGE,{"disambiguationData":[OSD([sQuery(id+"F58.wireOp",EDGE,"E216.trimOffspring")])],"isStart":true});
            var Q7;
            Q7=makeQuery(id+"F59.opExtrude","CAP_EDGE",EDGE,{"disambiguationData":[OSD([sQuery(id+"F58.wireOp",EDGE,"E220.trimOffspring")])],"isStart":true});
            var Q8;
            Q8=makeQuery(id+"F59.opExtrude","CAP_EDGE",EDGE,{"disambiguationData":[OSD([sQuery(id+"F58.wireOp",EDGE,"E222.trimOffspring")])],"isStart":true});
            var Q9;
            Q9=makeQuery(id+"F59.opExtrude","CAP_EDGE",EDGE,{"disambiguationData":[OSD([sQuery(id+"F58.wireOp",EDGE,"E223.trimOffspring")])],"isStart":true});
            var Q10;
            Q10=makeQuery(id+"F59.opExtrude","CAP_EDGE",EDGE,{"disambiguationData":[OSD([sQuery(id+"F58.wireOp",EDGE,"E221.trimOffspring")])],"isStart":true});
            var Q11;
            Q11=makeQuery(id+"F59.opExtrude","CAP_EDGE",EDGE,{"disambiguationData":[OSD([sQuery(id+"F58.wireOp",EDGE,"E215.trimOffspring")])],"isStart":true});
            var Q12;
            Q12=makeQuery(id+"F59.opExtrude","CAP_EDGE",EDGE,{"disambiguationData":[OSD([sQuery(id+"F58.wireOp",EDGE,"E191")])],"isStart":true});
            var Q13;
            Q13=makeQuery(id+"F59.opExtrude","CAP_EDGE",EDGE,{"disambiguationData":[OSD([sQuery(id+"F58.wireOp",EDGE,"E194.rect.top")])],"isStart":true});
            var Q14;
            Q14=makeQuery(id+"F59.opExtrude","CAP_EDGE",EDGE,{"disambiguationData":[OSD([sQuery(id+"F58.wireOp",EDGE,"E188")])],"isStart":true});
            var Q15;
            Q15=makeQuery(id+"F59.opExtrude","CAP_EDGE",EDGE,{"disambiguationData":[OSD([sQuery(id+"F58.wireOp",EDGE,"E214.trimOffspring")])],"isStart":true});
            var Q16;
            Q16=makeQuery(id+"F59.opExtrude","CAP_EDGE",EDGE,{"disambiguationData":[OSD([sQuery(id+"F58.wireOp",EDGE,"E206.trimOffspring")])],"isStart":true});
            var Q17;
            Q17=makeQuery(id+"F59.opExtrude","CAP_EDGE",EDGE,{"disambiguationData":[OSD([sQuery(id+"F58.wireOp",EDGE,"E204.trimOffspring")])],"isStart":true});
            var Q18;
            Q18=makeQuery(id+"F59.opExtrude","CAP_EDGE",EDGE,{"disambiguationData":[OSD([sQuery(id+"F58.wireOp",EDGE,"E207.trimOffspring")])],"isStart":true});
            var Q19;
            Q19=makeQuery(id+"F59.opExtrude","CAP_EDGE",EDGE,{"disambiguationData":[OSD([sQuery(id+"F58.wireOp",EDGE,"E196.trimOffspring")])],"isStart":true});
            var Q20;
            Q20=makeQuery(id+"F59.opExtrude","CAP_EDGE",EDGE,{"disambiguationData":[OSD([sQuery(id+"F58.wireOp",EDGE,"E197.trimOffspring")])],"isStart":true});
            var Q21;
            Q21=makeQuery(id+"F59.opExtrude","CAP_EDGE",EDGE,{"disambiguationData":[OSD([sQuery(id+"F58.wireOp",EDGE,"E199.trimOffspring")])],"isStart":true});
            var Q22;
            Q22=makeQuery(id+"F59.opExtrude","CAP_EDGE",EDGE,{"disambiguationData":[OSD([sQuery(id+"F58.wireOp",EDGE,"E198.trimOffspring")])],"isStart":true});
            var Q23;
            Q23=makeQuery(id+"F59.opExtrude","CAP_EDGE",EDGE,{"disambiguationData":[OSD([sQuery(id+"F58.wireOp",EDGE,"E193.rect.top")])],"isStart":true});
            var Q24;
            Q24=makeQuery(id+"F59.opExtrude","CAP_EDGE",EDGE,{"disambiguationData":[OSD([sQuery(id+"F58.wireOp",EDGE,"E208.trimOffspring")])],"isStart":true});
            var Q25;
            Q25=makeQuery(id+"F59.opExtrude","CAP_EDGE",EDGE,{"disambiguationData":[OSD([sQuery(id+"F58.wireOp",EDGE,"E193.rect.bottom")])],"isStart":true});
            var Q26;
            Q26=makeQuery(id+"F59.opExtrude","CAP_EDGE",EDGE,{"disambiguationData":[OSD([sQuery(id+"F58.wireOp",EDGE,"E209.trimOffspring")])],"isStart":true});
            var Q27;
            Q27=makeQuery(id+"F59.opExtrude","CAP_EDGE",EDGE,{"disambiguationData":[OSD([sQuery(id+"F58.wireOp",EDGE,"E190")])],"isStart":true});
            var Q28;
            Q28=makeQuery(id+"F59.opExtrude","CAP_EDGE",EDGE,{"disambiguationData":[OSD([sQuery(id+"F58.wireOp",EDGE,"E205.trimOffspring")])],"isStart":true});
            var Q29;
            Q29=makeQuery(id+"F59.opExtrude","CAP_EDGE",EDGE,{"disambiguationData":[OSD([sQuery(id+"F58.wireOp",EDGE,"E189")])],"isStart":true});
            var Q30;
            Q30=makeQuery(id+"F59.opExtrude","CAP_EDGE",EDGE,{"disambiguationData":[OSD([sQuery(id+"F58.wireOp",EDGE,"E192.rect.right")])],"isStart":true});
            fillet(context, id + "F60", {"entities" : qUnion([Q0, Q1, Q2, Q3, Q4, Q5, Q6, Q7, Q8, Q9, Q10, Q11, Q12, Q13, Q14, Q15, Q16, Q17, Q18, Q19, Q20, Q21, Q22, Q23, Q24, Q25, Q26, Q27, Q28, Q29, Q30]), "radius" : 60 * mm, "tangentPropagation" : true, "allowEdgeOverflow" : false});
        }
        {
            var Q0;
            Q0=makeQuery(id+"F1.opExtrude","SWEPT_FACE",FACE,{"disambiguationData":[OSD([sQuery(id+"F0.wireOp",EDGE,"E10.7")])]});
            var sketch = newSketch(context, id + "F61", { "sketchPlane" : qUnion([Q0])});
            skLineSegment(sketch, "E232", {"start": v(-7055.28, -342.74) * mm, "end": v(-6705.28, -32.74) * mm});
            skLineSegment(sketch, "E233", {"start": v(-6705.28, -32.74) * mm, "end": v(-6294.72, -32.74) * mm});
            skLineSegment(sketch, "E234", {"start": v(-6294.72, -32.74) * mm, "end": v(-6059.77, -312.74) * mm});
            skLineSegment(sketch, "E235", {"start": v(-6059.77, -312.74) * mm, "end": v(-890.23, -312.74) * mm});
            skLineSegment(sketch, "E236", {"start": v(-890.23, -312.74) * mm, "end": v(-655.28, -32.74) * mm});
            skLineSegment(sketch, "E237", {"start": v(-655.28, -32.74) * mm, "end": v(-244.72, -32.74) * mm});
            skLineSegment(sketch, "E238", {"start": v(-244.72, -32.74) * mm, "end": v(74.05, -255.94) * mm});
            skLineSegment(sketch, "E239.0", {"start": v(-251.03, -52.74) * mm, "end": v(62.58, -272.33) * mm});
            skLineSegment(sketch, "E239.1", {"start": v(-645.95, -52.74) * mm, "end": v(-251.03, -52.74) * mm});
            skLineSegment(sketch, "E239.2", {"start": v(-880.9, -332.74) * mm, "end": v(-645.95, -52.74) * mm});
            skLineSegment(sketch, "E239.3", {"start": v(-7042.02, -357.7) * mm, "end": v(-6697.7, -52.74) * mm});
            skLineSegment(sketch, "E239.4", {"start": v(-6697.7, -52.74) * mm, "end": v(-6304.05, -52.74) * mm});
            skLineSegment(sketch, "E239.5", {"start": v(-6304.05, -52.74) * mm, "end": v(-6069.1, -332.74) * mm});
            skLineSegment(sketch, "E239.6", {"start": v(-6069.1, -332.74) * mm, "end": v(-880.9, -332.74) * mm});
            skLineSegment(sketch, "E240", {"start": v(-7055.28, -342.74) * mm, "end": v(-7042.02, -357.7) * mm});
            skLineSegment(sketch, "E241", {"start": v(62.58, -272.33) * mm, "end": v(74.05, -255.94) * mm});
            skSolve(sketch);
        }
        {
            var Q0;
            Q0 = qSketchRegion(id + "F61", true);
            extrude(context, id + "F62", {"entities" : qUnion([Q0]), "endBound" : BoundingType.SYMMETRIC, "depth" : 230 * mm});
        }
        {
            var Q0;
            {var subQ0=sQuery(id+"F0.wireOp",EDGE,"E10.2");Q0=makeQuery(id+"F48.imprint","IMPRINT",FACE,{"disambiguationData":[TD([[makeQuery(id+"F48.imprint","IMPRINT",EDGE,{"derivedFrom":makeQuery(id+"F1.opExtrude","CAP_EDGE",EDGE,{"disambiguationData":[OSD([subQ0])],"isStart":true})}),1.0]])]});}
            var sketch = newSketch(context, id + "F63", { "sketchPlane" : qUnion([Q0])});
            skLineSegment(sketch, "E242", {"start": v(-74.02, -255.93) * mm, "end": v(244, -33.25) * mm});
            skLineSegment(sketch, "E243", {"start": v(244, -33.25) * mm, "end": v(660, -33.25) * mm});
            skLineSegment(sketch, "E244", {"start": v(660, -33.25) * mm, "end": v(920.12, -343.25) * mm});
            skLineSegment(sketch, "E245", {"start": v(920.12, -343.25) * mm, "end": v(6034.6, -343.25) * mm});
            skLineSegment(sketch, "E246", {"start": v(6034.6, -343.25) * mm, "end": v(6294.72, -33.25) * mm});
            skLineSegment(sketch, "E247", {"start": v(6294.72, -33.25) * mm, "end": v(6705.28, -33.25) * mm});
            skLineSegment(sketch, "E248", {"start": v(6705.28, -33.25) * mm, "end": v(7055.38, -342.87) * mm});
            skLineSegment(sketch, "E249.0", {"start": v(6697.7, -53.25) * mm, "end": v(7042.13, -357.86) * mm});
            skLineSegment(sketch, "E249.1", {"start": v(6304.05, -53.25) * mm, "end": v(6697.7, -53.25) * mm});
            skLineSegment(sketch, "E249.2", {"start": v(6043.93, -363.25) * mm, "end": v(6304.05, -53.25) * mm});
            skLineSegment(sketch, "E249.3", {"start": v(-62.55, -272.32) * mm, "end": v(250.3, -53.25) * mm});
            skLineSegment(sketch, "E249.4", {"start": v(250.3, -53.25) * mm, "end": v(650.67, -53.25) * mm});
            skLineSegment(sketch, "E249.5", {"start": v(650.67, -53.25) * mm, "end": v(910.8, -363.25) * mm});
            skLineSegment(sketch, "E249.6", {"start": v(910.8, -363.25) * mm, "end": v(6043.93, -363.25) * mm});
            skLineSegment(sketch, "E250", {"start": v(-74.02, -255.93) * mm, "end": v(-62.55, -272.32) * mm});
            skLineSegment(sketch, "E251", {"start": v(7055.38, -342.87) * mm, "end": v(7042.13, -357.86) * mm});
            skSolve(sketch);
        }
        {
            var Q0;
            Q0 = qSketchRegion(id + "F63", true);
            extrude(context, id + "F64", {"entities" : qUnion([Q0]), "endBound" : BoundingType.SYMMETRIC, "depth" : 220 * mm});
        }
        {
            var Q0;
            Q0=qCreatedBy(makeId("Right.planeOp"),FACE);
            var sketch = newSketch(context, id + "F65", { "sketchPlane" : qUnion([Q0])});
            skCircle(sketch, "E252", {"center": v(-450, -423.25) * mm, "radius": 45 * mm});
            skCircle(sketch, "E253", {"center": v(-6500, -423.25) * mm, "radius": 45 * mm});
            skSolve(sketch);
        }
        {
            var Q0;
            Q0 = qSketchRegion(id + "F65", true);
            extrude(context, id + "F66", {"entities" : qUnion([Q0]), "endBound" : BoundingType.SYMMETRIC, "depth" : 1430.7 * mm});
        }
    });
